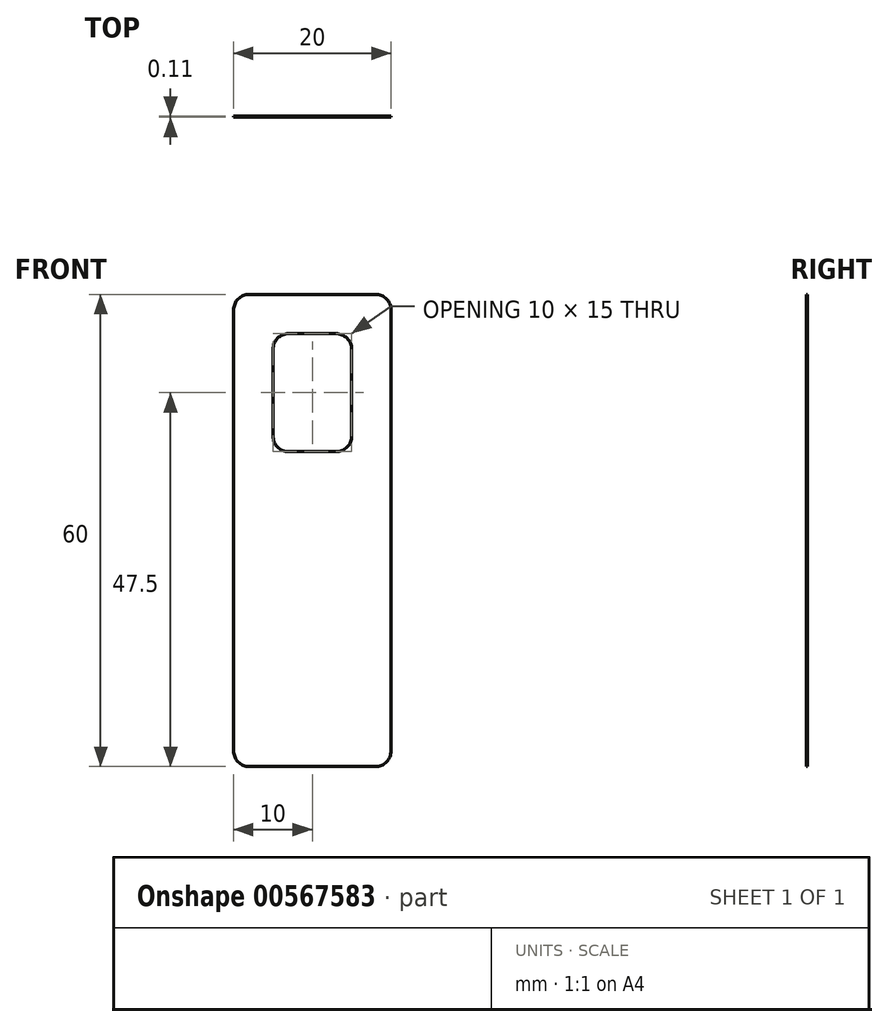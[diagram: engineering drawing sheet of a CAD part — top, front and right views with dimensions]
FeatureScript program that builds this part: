
annotation { "Feature Type Name" : "Feature", "Feature Type Description" : "" }
export const myFeature = defineFeature(function(context is Context, id is Id, definition is map)
    precondition{}
    {
        {
            var Q0;
            Q0=qCreatedBy(makeId("Front.planeOp"),FACE);
            var sketch = newSketch(context, id + "F0", { "sketchPlane" : qUnion([Q0])});
            skLineSegment(sketch, "E0.bottom", {"start": v(2, 0) * mm, "end": v(18, 0) * mm});
            skLineSegment(sketch, "E0.top", {"start": v(2, -60) * mm, "end": v(18, -60) * mm});
            skLineSegment(sketch, "E0.left", {"start": v(0, -2) * mm, "end": v(0, -58) * mm});
            skLineSegment(sketch, "E0.right", {"start": v(20, -2) * mm, "end": v(20, -58) * mm});
            skPoint(sketch, "E1.visualSharp", {"position": v(0, 0) * mm});
            skArc(sketch, "E1.filletArc", {"start": v(2, 0) * mm, "mid": v(0.59, -0.59) * mm, "end": v(0, -2) * mm});
            skPoint(sketch, "E2.visualSharp", {"position": v(20, 0) * mm});
            skArc(sketch, "E2.filletArc", {"start": v(20, -2) * mm, "mid": v(19.41, -0.59) * mm, "end": v(18, 0) * mm});
            skPoint(sketch, "E3.visualSharp", {"position": v(0, -60) * mm});
            skArc(sketch, "E3.filletArc", {"start": v(0, -58) * mm, "mid": v(0.59, -59.41) * mm, "end": v(2, -60) * mm});
            skPoint(sketch, "E4.visualSharp", {"position": v(20, -60) * mm});
            skArc(sketch, "E4.filletArc", {"start": v(18, -60) * mm, "mid": v(19.41, -59.41) * mm, "end": v(20, -58) * mm});
            skLineSegment(sketch, "E5.bottom", {"start": v(7, -5) * mm, "end": v(13, -5) * mm});
            skLineSegment(sketch, "E5.top", {"start": v(7, -20) * mm, "end": v(13, -20) * mm});
            skLineSegment(sketch, "E5.left", {"start": v(5, -7) * mm, "end": v(5, -18) * mm});
            skLineSegment(sketch, "E5.right", {"start": v(15, -7) * mm, "end": v(15, -18) * mm});
            skPoint(sketch, "E6.visualSharp", {"position": v(5, -5) * mm});
            skArc(sketch, "E6.filletArc", {"start": v(7, -5) * mm, "mid": v(5.59, -5.59) * mm, "end": v(5, -7) * mm});
            skPoint(sketch, "E7.visualSharp", {"position": v(15, -5) * mm});
            skArc(sketch, "E7.filletArc", {"start": v(15, -7) * mm, "mid": v(14.41, -5.59) * mm, "end": v(13, -5) * mm});
            skPoint(sketch, "E8.visualSharp", {"position": v(15, -20) * mm});
            skArc(sketch, "E8.filletArc", {"start": v(13, -20) * mm, "mid": v(14.41, -19.41) * mm, "end": v(15, -18) * mm});
            skPoint(sketch, "E9.visualSharp", {"position": v(5, -20) * mm});
            skArc(sketch, "E9.filletArc", {"start": v(5, -18) * mm, "mid": v(5.59, -19.41) * mm, "end": v(7, -20) * mm});
            skSolve(sketch);
        }
        {
            var Q0;
            Q0=makeQuery(id+"F0.imprint","IMPRINT",FACE,{"disambiguationData":[TD([[makeQuery(id+"F0.imprint","IMPRINT",EDGE,{"derivedFrom":sQuery(id+"F0.wireOp",EDGE,"E0.bottom")}),-1.0]])]});
            extrude(context, id + "F1", {"entities" : qUnion([Q0]), "depth" : 0.1 * mm, "offsetDistance" : 25 * mm});
        }
    });
